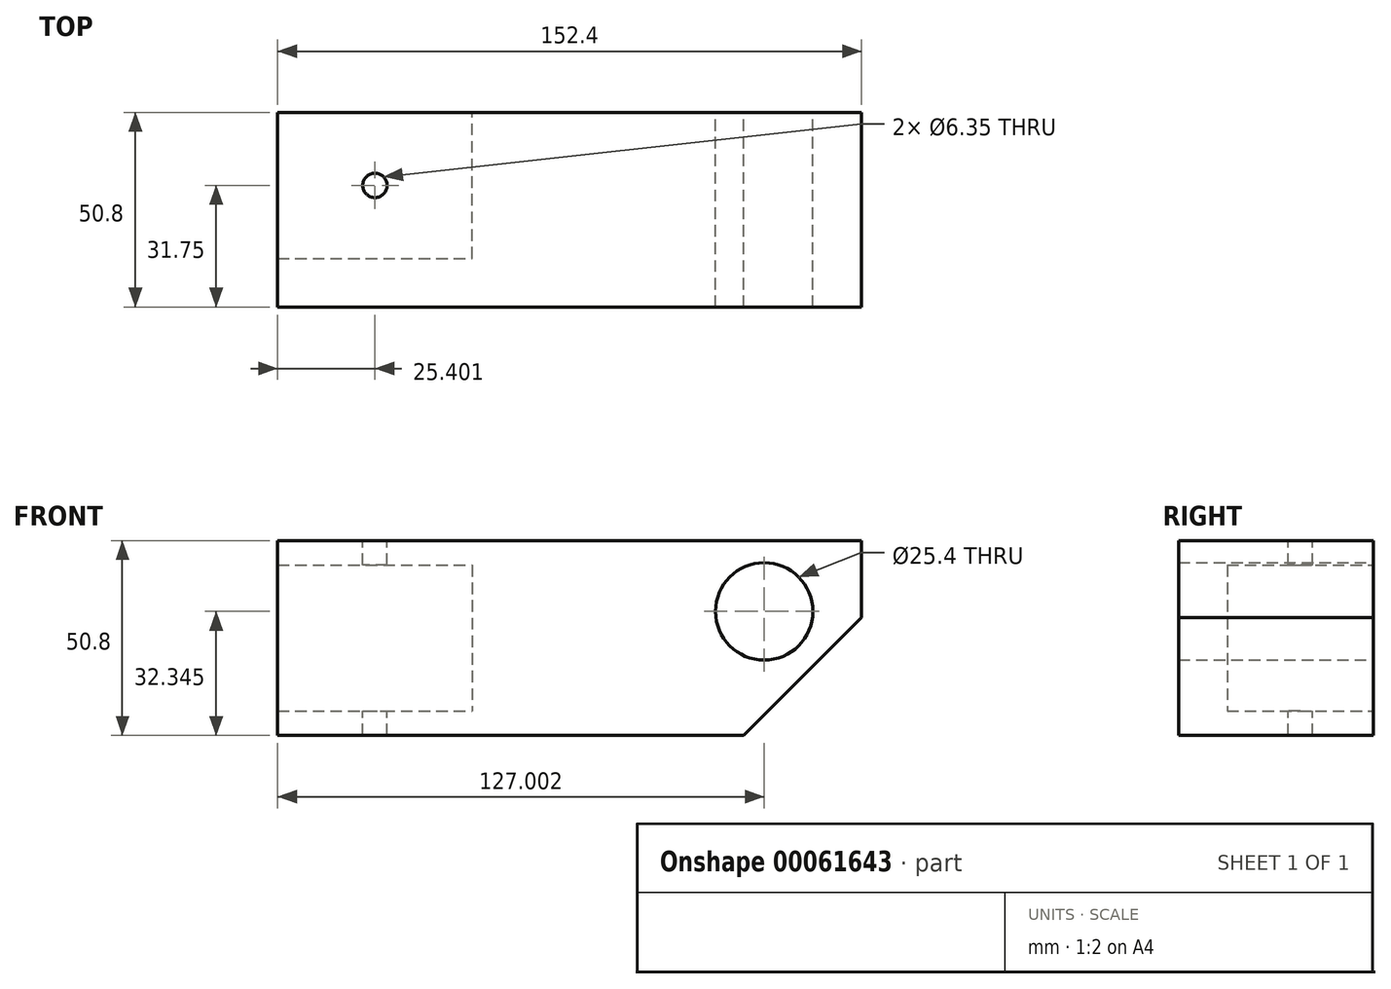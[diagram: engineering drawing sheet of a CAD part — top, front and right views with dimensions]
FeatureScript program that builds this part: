
annotation { "Feature Type Name" : "Feature", "Feature Type Description" : "" }
export const myFeature = defineFeature(function(context is Context, id is Id, definition is map)
    precondition{}
    {
        {
            var Q0;
            Q0=qCreatedBy(makeId("Front.planeOp"),FACE);
            var sketch = newSketch(context, id + "F0", { "sketchPlane" : qUnion([Q0])});
            skLineSegment(sketch, "E0", {"start": v(-140.8, 30.32) * mm, "end": v(-90, 30.32) * mm});
            skLineSegment(sketch, "E1", {"start": v(-90, 30.32) * mm, "end": v(-90, -7.78) * mm});
            skLineSegment(sketch, "E2", {"start": v(-90, -7.78) * mm, "end": v(-140.8, -7.78) * mm});
            skLineSegment(sketch, "E3", {"start": v(-140.8, -7.78) * mm, "end": v(-140.8, -14.13) * mm});
            skLineSegment(sketch, "E4", {"start": v(-140.8, -14.13) * mm, "end": v(-19.2, -14.13) * mm});
            skLineSegment(sketch, "E5", {"start": v(-19.2, -14.13) * mm, "end": v(11.6, 16.67) * mm});
            skLineSegment(sketch, "E6", {"start": v(11.6, 16.67) * mm, "end": v(11.6, 36.67) * mm});
            skLineSegment(sketch, "E7", {"start": v(11.6, 36.67) * mm, "end": v(-140.8, 36.67) * mm});
            skLineSegment(sketch, "E8", {"start": v(-140.8, 36.67) * mm, "end": v(-140.8, 30.32) * mm});
            skSolve(sketch);
        }
        {
            var Q0;
            Q0=makeQuery(id+"F0.imprint","IMPRINT",FACE,{"disambiguationData":[TD([[makeQuery(id+"F0.imprint","IMPRINT",EDGE,{"derivedFrom":sQuery(id+"F0.wireOp",EDGE,"E0")}),1.0]])]});
            extrude(context, id + "F1", {"entities" : qUnion([Q0]), "depth" : 50.8 * mm});
        }
        {
            var Q0;
            Q0=makeQuery(id+"F1.opExtrude","SWEPT_FACE",FACE,{"disambiguationData":[OSD([sQuery(id+"F0.wireOp",EDGE,"E1")])]});
            var sketch = newSketch(context, id + "F2", { "sketchPlane" : qUnion([Q0])});
            skLineSegment(sketch, "E9.bottom", {"start": v(38.1, 30.32) * mm, "end": v(50.8, 30.32) * mm});
            skLineSegment(sketch, "E9.top", {"start": v(38.1, -7.78) * mm, "end": v(50.8, -7.78) * mm});
            skLineSegment(sketch, "E9.left", {"start": v(38.1, 30.32) * mm, "end": v(38.1, -7.78) * mm});
            skLineSegment(sketch, "E9.right", {"start": v(50.8, 30.32) * mm, "end": v(50.8, -7.78) * mm});
            skSolve(sketch);
        }
        {
            var Q0;
            Q0=makeQuery(id+"F2.imprint","IMPRINT",FACE,{"disambiguationData":[TD([[makeQuery(id+"F2.imprint","IMPRINT",EDGE,{"derivedFrom":sQuery(id+"F2.wireOp",EDGE,"E9.bottom")}),1.0]])]});
            extrude(context, id + "F3", {"entities" : qUnion([Q0]), "operationType" : NewBodyOperationType.ADD, "depth" : 50.8 * mm});
        }
        {
            var Q0;
            Q0=makeQuery(id+"F1.opExtrude","CAP_FACE",FACE,{"disambiguationData":[OSD([sQuery(id+"F0.wireOp",EDGE,"E0"),sQuery(id+"F0.wireOp",EDGE,"E1"),sQuery(id+"F0.wireOp",EDGE,"E2"),sQuery(id+"F0.wireOp",EDGE,"E3"),sQuery(id+"F0.wireOp",EDGE,"E4"),sQuery(id+"F0.wireOp",EDGE,"E5"),sQuery(id+"F0.wireOp",EDGE,"E6"),sQuery(id+"F0.wireOp",EDGE,"E7"),sQuery(id+"F0.wireOp",EDGE,"E8")])],"isStart":true});
            var sketch = newSketch(context, id + "F4", { "sketchPlane" : qUnion([Q0])});
            skPoint(sketch, "E10", {"position": v(13.8, 18.22) * mm});
            skSolve(sketch);
        }
        {
            var Q0;
            Q0=sQuery(id+"F4.wireOp",VERTEX,"E10");
            var Q1;
            Q1=makeQuery(id+"F1.opExtrude","SWEPT_BODY",BODY,{"disambiguationData":[OSD([sQuery(id+"F0.wireOp",EDGE,"E0"),sQuery(id+"F0.wireOp",EDGE,"E1"),sQuery(id+"F0.wireOp",EDGE,"E2"),sQuery(id+"F0.wireOp",EDGE,"E3"),sQuery(id+"F0.wireOp",EDGE,"E4"),sQuery(id+"F0.wireOp",EDGE,"E5"),sQuery(id+"F0.wireOp",EDGE,"E6"),sQuery(id+"F0.wireOp",EDGE,"E7"),sQuery(id+"F0.wireOp",EDGE,"E8")])]});
            hole(context, id + "F5", {"style" : HoleStyle.SIMPLE, "holeDiameter" : 25.4 * mm, "endStyle" : HoleEndStyle.THROUGH, "locations" : qUnion([Q0]), "scope" : qUnion([Q1])});
        }
        {
            var Q0;
            Q0=makeQuery(id+"F1.opExtrude","SWEPT_FACE",FACE,{"disambiguationData":[OSD([sQuery(id+"F0.wireOp",EDGE,"E7")])]});
            var sketch = newSketch(context, id + "F6", { "sketchPlane" : qUnion([Q0])});
            skPoint(sketch, "E11", {"position": v(-115.4, -19.05) * mm});
            skSolve(sketch);
        }
        {
            var Q0;
            Q0=sQuery(id+"F6.wireOp",VERTEX,"16b47177-ccb6-458a-998a-ef716eb27e59");
            var Q1;
            Q1=sQuery(id+"F6.wireOp",VERTEX,"E11");
            var Q2;
            Q2=makeQuery(id+"F1.opExtrude","SWEPT_BODY",BODY,{"disambiguationData":[OSD([sQuery(id+"F0.wireOp",EDGE,"E0"),sQuery(id+"F0.wireOp",EDGE,"E1"),sQuery(id+"F0.wireOp",EDGE,"E2"),sQuery(id+"F0.wireOp",EDGE,"E3"),sQuery(id+"F0.wireOp",EDGE,"E4"),sQuery(id+"F0.wireOp",EDGE,"E5"),sQuery(id+"F0.wireOp",EDGE,"E6"),sQuery(id+"F0.wireOp",EDGE,"E7"),sQuery(id+"F0.wireOp",EDGE,"E8")])]});
            hole(context, id + "F7", {"style" : HoleStyle.SIMPLE, "holeDiameter" : 6.35 * mm, "endStyle" : HoleEndStyle.THROUGH, "locations" : qUnion([Q0, Q1]), "scope" : qUnion([Q2])});
        }
    });
